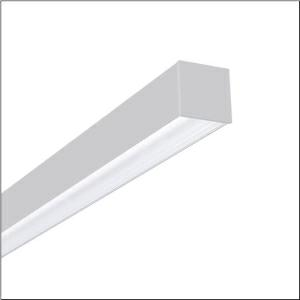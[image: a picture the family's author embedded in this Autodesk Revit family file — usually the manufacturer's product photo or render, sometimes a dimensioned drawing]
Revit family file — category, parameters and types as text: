
# Revit family: silica_r_5mx21dd1w4a_969a
name_source: partatom
category: Lighting Fixtures
units: mm (PartAtom-declared; Revit-internal decimal feet)

## family parameters
Cut with Voids When Loaded = No
Host = Face
Light Source = No
Part Type = Normal
Room Calculation Point = No
Round Connector Dimension = Use Diameter
Shared = No

## types (1)
- --- (1 x LED, 3140 lm, 22.6 W, 4000K)
    Apparent Load = 23 VA
    CIE Flux Codes = 47 79 96 100 100
    Color Rendering = 80
    Color Temperature = 4000K
    Default Elevation = 1800 mm
    Description = Silica®, office luminaire, of aluminium, opal, light emission: direct distribution, primary light characteristic: symmetric, installation type: surface-mounted, LED, rated luminous flux: 3.010lm, luminous efficacy: 123lm/W, light colour: 840, colour temperature: 4000K, control gear: ECG DALI, with terminal, 3+2-pole, max. 2.5mm², mains connection: 230V, AC, 50/60Hz, rated input power: 24W, luminaire housing, of aluminium, traffic white (RAL 9016), length: 1.442mm, width: 65mm, height: 64mm, protection rating (complete): IP20, insulation class (complete): insulation class I (protective earthing), certification: CE, permissible operating ambient temperature: 0..+35°C, standard: EN 50419, packaging unit: 1 piece
    Height = 64 mm
    Lamp = 1 x LED
    Lamp Light Flux = 3140 lm
    Lamp Power = 22.6 W
    Lamp count = 1
    Length = 1442 mm
    Luminous efficacy = 139 lm/W
    Manufacturer = Siteco
    ModVariant = No
    Model = 5MX21DD1W4A
    Mounting Place = Ceiling
    Mounting Type = Surface mounted
    Number of Poles = 1
    OnlyDefault = Yes
    Power Factor = 1
    Product Name = Silica®
    Product group = office luminaire | ceiling mounted
    ProductGroupID = 304
    Protection Class = Protection class I
    Protection Degree = IP 20
    RLX_Detail_Level = 1
    RLX_Emergency_Light_Flux = 0 lm
    RLX_Emergency_Type = 0
    RLX_Emergency_Type_DB = No
    RlxData = <blob elided: 22713 chars, md5=a0dd39e0>
    Socket = socket
    Standby Power = 0 W
    System Light Flux = 3140 lm
    System Power = 23 W
    Type Comments = factory setting: luminous flux: 100 % | dim-lin: 254 | 125 mA
    Type Image = l_248206.jpg
    URL = http://relux.com
    VarID = @adj_135405
    Voltage = 0 V
    Weight = 0.00 kg
    Width = 65 mm

## geometry (parser evidence)
native form markers: Blend x4, Sweep x9
no freeform markers — native parametric forms only
